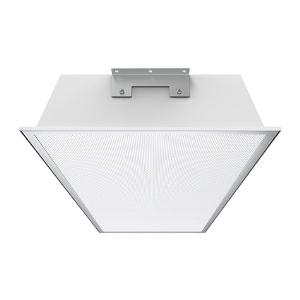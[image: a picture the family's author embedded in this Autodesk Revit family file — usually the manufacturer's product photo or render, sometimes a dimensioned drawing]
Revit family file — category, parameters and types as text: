
# Revit family: 3f_filippi_-_beta_500_sp_3f_filippi_-_52057_-_beta_500_150w-840_dali_sp_l870
name_source: partatom
category: Lighting Fixtures
units: mm (PartAtom-declared; Revit-internal decimal feet)

## family parameters
Cut with Voids When Loaded = No
Host = Face
Light Source = No
Part Type = Normal
Room Calculation Point = No
Round Connector Dimension = Use Diameter
Shared = No

## types (1)
- 3F Filippi - Beta 500 SP (1 x LED, 25040 lm, 162 W, 4000 K)
    Apparent Load = 162 VA
    Approval mark = CE
    CIE Flux Codes = 62 89 97 100 100
    Color Rendering = 80
    Color Temperature = 4000 K
    Control Gear = Electronic transformer
    Default Elevation = 1800 mm
    Description = ILLUMINOTECHNICAL
Luminous efficiency 100% (DLOR 100%, ULOR 0%).
Initial luminous flux of the luminaire 25040 lm.
Direct symmetric medium distribution.
Installation Interdistance Transv.D = 1.25 x hu - Long.D = 1.25 x hu.
Tabular UGR (CIE 117 - 4H-8H; S=0.25H; 70/50/20): RUG 23.6 - 23.7.
Beam angle: 87° - 91°.
Luminous efficacy 155 lm/W.
Lifetime (L93/B10): 30000 h. (tq+25°C)
Lifetime (L90/B10): 50000 h. (tq+25°C)
Lifetime (L85/B10): 80000 h. (tq+25°C)
Lifetime (L80/B10): 100000 h. (tq+25°C)
Lifetime (L85/B10): 50000 h. (tq+50°C)
Sudden decreased luminous flux after 50000 hours: 0% (C0).
Photobiological safety in compliance with IEC/TR 62778: RG0 risk exempt, (IEC 62471).
In compliance with IEC/EN 62722-2-1 - IEC/EN 62717 standards.

SOURCE
3 linear LED modules 52W/840.
Energy efficiency class (UE 2019/2020 - UE 2019/2015): C.
CIE 13.3 Colour rendering index: CRI >80 (R9 <50%).
IES TM-30 Fidelity Index: Rf = 84 Rg = 95.
CCT nominal colour temperature 4000 K.
Colour initial tolerance (MacAdam): SDCM 3.

MECHANICAL
Housing in white painted epoxy-polyester powder aluminium.
White aluminium non-iridescent high efficiency.
SP transparent methacrylate (PMMA) diffuser, prismatic outside, antiglare.
Perimetrical frame in stainless steel with vandal-proof opening and stainless steel nuts and bolts.
Polyurethane foam seal, ecological, anti-aging, installed using a continuous automatic process with no joints.
Fixing bracket in stainless steel.
Luminaire with limited surface temperature. - D - (EN 60598-2-24)
Dimensions: 870x515 mm, height 105 mm. Weight 8.295 kg.
IP66 protection degree.
Mechanical strength to impacts IK07 (2 joule).
Glow-wire test resistance 850°C.

ELECTRICAL
Halogen Free DALI-2 DATI (Parts 251, 252, 253), PUSH-DIM, electronic wiring 230V-50/60Hz, power factor 0.95 at full load, THD <25%, constant output current, class I, 1 driver, 1 DALI addresse.
Power of the luminaire 162 W.
ENEC - CE.
SAFE FLICKER: PstLM=<1 and SVM=<0.4 (IEC TR 61547-1 and IEC TR 63158), to ensure a more comfortable and safe light.
Luminaire compliant with EN 60598-2-22 for power supply from a centralised emergency system CPSS (Central Power Supply System), not incorporated in the luminaire - high risk areas excluded. The default power and flux are 100% in AC and 15% in DC.
Ambient temperature from -20°C to +50°C.
Temperature class T6 max 85°C.
Quick connection via M25 5P connector with 9-13 mm tightening range.
Quick connection in polycarbonate with M20x1,5 cable gland, to access the terminal block positioned on a removable runner.
Relative humidity UR: <85%.

INSTALLATION
Ceiling / Suspended.
All accessories dedicated to this product are available on the Catalog and on our website www.3F-Filippi.com.

APPLICATIONS
Suitable product for food production plants (HACCP), IFS (Food Version 6), BRC (GSFS Food Version 7).
Commercial and industrial environments and warehouses.

LIGHT MANAGEMENT
Recommended minimum setting: 10%.
The luminaire, equipped with (DALI-2 DATI) driver, can be controlled manually with 3F Easy Dim technology or automatically/manually with wired or wireless DALI/D2D control systems.
The D2D driver guarantees interoperability with other devices with the same certification by making the following information available:
Device Data (Part 251), Energy Report (Part 252), Diagnosis & Maintenance (Part 253).
In electrical systems without a regulation system (manual or automatic) and DALI bus, a suitable jumper must be made on the DA-DA terminals of the appliance.

WARNING
Fixture not suitable for cold stores with an ambient temperature <0°C and/or relative humidity >85%.
Luminaire designed for disposal/recycling at end-of-life.
Replaceable (LED only) light source by a professional. Replaceable control gear by a professional.
    Height = 105 mm
    Lamp = 1 x LED
    Lamp Light Flux = 25040 lm
    Lamp Power = 162 W
    Lamp count = 1
    Length = 870 mm
    Lifetime = 50000 h
    Luminous efficacy = 155 lm/W
    Manufacturer = 3F Filippi
    ModVariant = No
    Model = 3F Filippi - 52057 - Beta 500 150W-840 DALI SP L870
    Mounting Place = Ceiling
    Mounting Type = Pendant
    Number of Poles = 1
    OnlyDefault = Yes
    Power Factor = 1
    Product Name = 3F Filippi - Beta 500 SP
    Product group = pendant luminaire
    ProductGroupID = 9
    Protection Class = Protection class I
    Protection Degree = IP 66
    RLX_Detail_Level = 1
    RLX_Emergency_Light_Flux = 0 lm
    RLX_Emergency_Type = 0
    RLX_Emergency_Type_DB = No
    RlxData = <blob elided: 135513 chars, md5=d44418f6>
    Socket = socket
    Standby Power = 0 W
    System Light Flux = 25040 lm
    System Power = 162 W
    Type Comments = Product without accessories
    Type Image = 3ffilippi_beta_500_sp_pc.jpg
    URL = http://relux.com
    VarID = ---
    Voltage = 0 V
    Weight = 0.00 kg
    Width = 515 mm

## geometry (parser evidence)
native form markers: Blend x4, Sweep x9
no freeform markers — native parametric forms only
